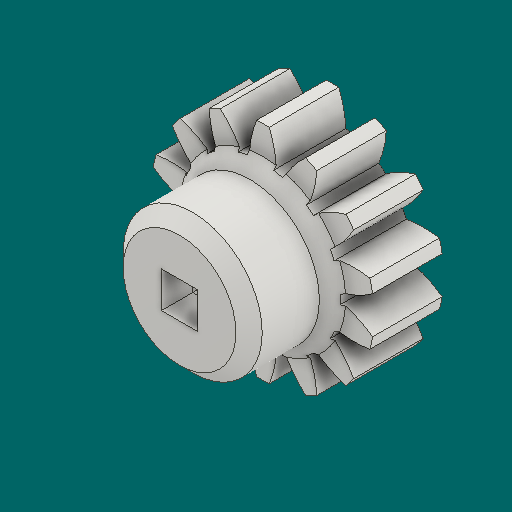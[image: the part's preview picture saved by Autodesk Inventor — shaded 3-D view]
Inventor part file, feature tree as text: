
AUTODESK INVENTOR PART (.ipt)
format: ipt  version: 2023.1 (Build 271208000, 208)  size: 356,864 bytes
history: native  units: mm (DEFAULTED — no unit token found)
features: sketch x5, extrude x4, plane x4, other x3, chamfer x3, projected_geometry x1
ambient origin geometry x8: Origin, YZ Plane, XZ Plane, XY Plane, X Axis, Y Axis, Z Axis, Center Point
bodies: Solid1 (feature_tree)
feature tree (20):
  extrude  "Extrusion1"  Depth=6.35mm TaperAngle=0.0deg
  plane  "Work Plane1"
  plane  "Work Plane2"
  plane  "Work Plane3"
  other  "Spur Gear"
  extrude  "Extrusion2"  Depth=76.2mm TaperAngle=0.0deg
  sketch  "Sketch4"  dims[d14=0.0mm]
  plane  "Work Plane4"
  extrude  "Extrusion3"  TaperAngle=0.0deg  [1 undecoded]
  chamfer  "Chamfer1"  [1 undecoded]
  chamfer  "Chamfer2"  [1 undecoded]
  extrude  "Extrusion4"  TaperAngle=0.0deg  [1 undecoded]
  chamfer  "Chamfer3"  Distance=17.78mm
  sketch  "Sketch1"  dims[d0=20.32mm d1=6.35mm d2=0.0mm]
  sketch  "Sketch2"  dims[d3=17.78mm d4=76.2mm d5=0.0mm]
  other  "Srf1"
  sketch  "Sketch3"  dims[d6=0.0mm d7=2.243995mm d9=0.0mm]
  projected_geometry  "Projected Loop1"
  sketch  "Sketch5"  dims[d15=17.78mm d16=0.0mm d17=0.0mm d18=0.0mm d19=17.78mm d20=3.302mm d21=3.302mm d22=0.0mm d23=0.0mm d24=12.7mm d25=7.62mm d26=0.0mm d27=1.2mm d28=3.175mm d29=45.0deg d30=1.2mm d31=3.175mm d32=45.0deg d33=6.604mm d34=6.604mm d35=11.1125mm d36=0.0mm d37=1.651mm d38=3.175mm d39=45.0deg]
  other  "Pitch Diameter"
note: 4 required parameter values undecoded (feature->parameter linkage not recoverable at this tier; creation-order binding heuristic only, values carry confidence <= 0.55)
